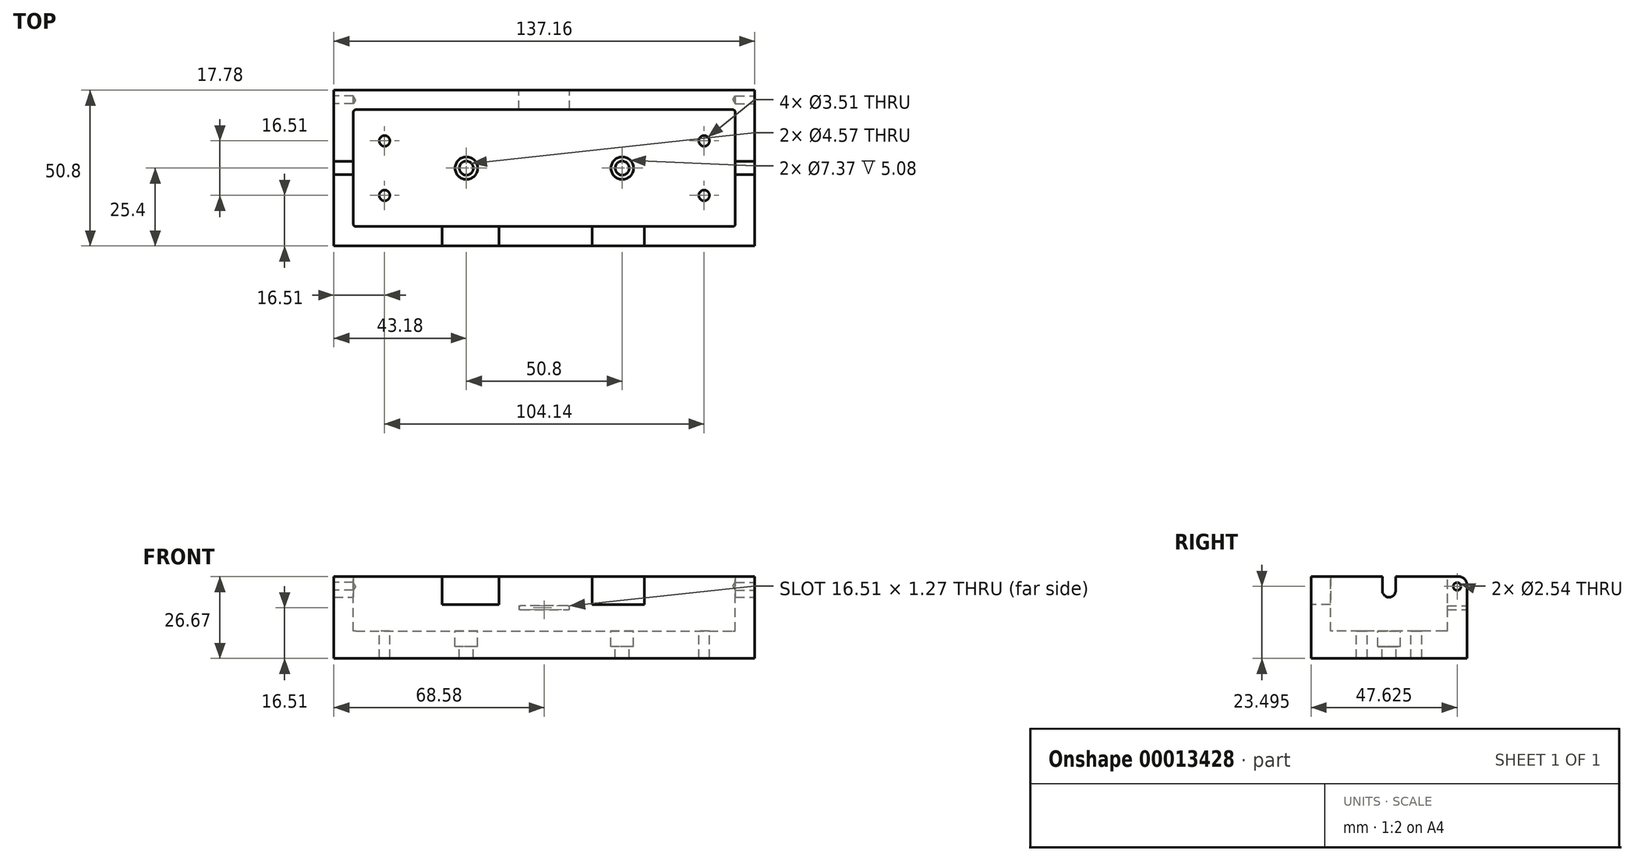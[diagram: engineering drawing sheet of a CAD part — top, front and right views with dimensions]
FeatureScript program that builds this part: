
annotation { "Feature Type Name" : "Feature", "Feature Type Description" : "" }
export const myFeature = defineFeature(function(context is Context, id is Id, definition is map)
    precondition{}
    {
        {
            var Q0;
            Q0=qCreatedBy(makeId("Top.planeOp"),FACE);
            var sketch = newSketch(context, id + "F0", { "sketchPlane" : qUnion([Q0])});
            skLineSegment(sketch, "E0.bottom", {"start": v(0, 50.8) * mm, "end": v(137.16, 50.8) * mm});
            skLineSegment(sketch, "E0.top", {"start": v(0, 0) * mm, "end": v(137.16, 0) * mm});
            skLineSegment(sketch, "E0.left", {"start": v(0, 50.8) * mm, "end": v(0, 0) * mm});
            skLineSegment(sketch, "E0.right", {"start": v(137.16, 50.8) * mm, "end": v(137.16, 0) * mm});
            skSolve(sketch);
        }
        {
            var Q0;
            Q0 = qSketchRegion(id + "F0", true);
            extrude(context, id + "F1", {"entities" : qUnion([Q0]), "depth" : 26.67 * mm});
        }
        {
            var Q0;
            Q0=makeQuery(id+"F1.opExtrude","CAP_FACE",FACE,{"disambiguationData":[OSD([sQuery(id+"F0.wireOp",EDGE,"E0.bottom"),sQuery(id+"F0.wireOp",EDGE,"E0.top"),sQuery(id+"F0.wireOp",EDGE,"E0.left"),sQuery(id+"F0.wireOp",EDGE,"E0.right")])],"isStart":false});
            var sketch = newSketch(context, id + "F2", { "sketchPlane" : qUnion([Q0])});
            skLineSegment(sketch, "E1.bottom", {"start": v(7.16, 44.45) * mm, "end": v(130, 44.45) * mm});
            skLineSegment(sketch, "E1.top", {"start": v(7.16, 6.35) * mm, "end": v(130, 6.35) * mm});
            skLineSegment(sketch, "E1.left", {"start": v(6.35, 43.64) * mm, "end": v(6.35, 7.16) * mm});
            skLineSegment(sketch, "E1.right", {"start": v(130.8, 43.64) * mm, "end": v(130.8, 7.16) * mm});
            skPoint(sketch, "E2.visualSharp", {"position": v(6.35, 44.45) * mm});
            skArc(sketch, "E2.filletArc", {"start": v(7.16, 44.45) * mm, "mid": v(6.59, 44.21) * mm, "end": v(6.35, 43.64) * mm});
            skPoint(sketch, "E3.visualSharp", {"position": v(6.35, 6.35) * mm});
            skArc(sketch, "E3.filletArc", {"start": v(6.35, 7.16) * mm, "mid": v(6.59, 6.59) * mm, "end": v(7.16, 6.35) * mm});
            skPoint(sketch, "E4.visualSharp", {"position": v(130.8, 44.45) * mm});
            skArc(sketch, "E4.filletArc", {"start": v(130.8, 43.64) * mm, "mid": v(130.57, 44.21) * mm, "end": v(130, 44.45) * mm});
            skPoint(sketch, "E5.visualSharp", {"position": v(130.8, 6.35) * mm});
            skArc(sketch, "E5.filletArc", {"start": v(130, 6.35) * mm, "mid": v(130.57, 6.59) * mm, "end": v(130.8, 7.16) * mm});
            skSolve(sketch);
        }
        {
            var Q0;
            Q0 = qSketchRegion(id + "F2", true);
            extrude(context, id + "F3", {"entities" : qUnion([Q0]), "operationType" : NewBodyOperationType.REMOVE, "oppositeDirection" : true, "depth" : 17.78 * mm});
        }
        {
            var Q0;
            Q0=makeQuery(id+"F1.opExtrude","SWEPT_FACE",FACE,{"disambiguationData":[OSD([sQuery(id+"F0.wireOp",EDGE,"E0.right")])]});
            var sketch = newSketch(context, id + "F4", { "sketchPlane" : qUnion([Q0])});
            skArc(sketch, "E6", {"start": v(23.24, 22.1) * mm, "mid": v(25.4, 19.94) * mm, "end": v(27.56, 22.1) * mm});
            skLineSegment(sketch, "E7.top", {"start": v(27.56, 26.67) * mm, "end": v(23.24, 26.67) * mm});
            skLineSegment(sketch, "E7.left", {"start": v(27.56, 22.1) * mm, "end": v(27.56, 26.67) * mm});
            skLineSegment(sketch, "E7.right", {"start": v(23.24, 22.1) * mm, "end": v(23.24, 26.67) * mm});
            skSolve(sketch);
        }
        {
            var Q0;
            Q0 = qSketchRegion(id + "F4", true);
            extrude(context, id + "F5", {"entities" : qUnion([Q0]), "operationType" : NewBodyOperationType.REMOVE, "endBound" : BoundingType.THROUGH_ALL, "oppositeDirection" : true, "depth" : 25.4 * mm});
        }
        {
            var Q0;
            Q0=makeQuery(id+"F3.boolean.opBoolean","COPY",FACE,{"derivedFrom":makeQuery(id+"F3.opExtrude","CAP_FACE",FACE,{"disambiguationData":[OSD([sQuery(id+"F2.wireOp",EDGE,"E1.bottom"),sQuery(id+"F2.wireOp",EDGE,"E1.top"),sQuery(id+"F2.wireOp",EDGE,"E1.left"),sQuery(id+"F2.wireOp",EDGE,"E1.right"),sQuery(id+"F2.wireOp",EDGE,"E2.filletArc"),sQuery(id+"F2.wireOp",EDGE,"E3.filletArc"),sQuery(id+"F2.wireOp",EDGE,"E4.filletArc"),sQuery(id+"F2.wireOp",EDGE,"E5.filletArc")])],"isStart":false})});
            var sketch = newSketch(context, id + "F6", { "sketchPlane" : qUnion([Q0])});
            skPoint(sketch, "E8", {"position": v(16.51, 34.29) * mm});
            skPoint(sketch, "E9", {"position": v(16.51, 16.5) * mm});
            skPoint(sketch, "E10", {"position": v(120.65, 16.51) * mm});
            skPoint(sketch, "E11", {"position": v(120.65, 34.3) * mm});
            skSolve(sketch);
        }
        {
            var Q0;
            Q0=sQuery(id+"F6.wireOp",VERTEX,"E8");
            var Q1;
            Q1=sQuery(id+"F6.wireOp",VERTEX,"E9");
            var Q2;
            Q2=sQuery(id+"F6.wireOp",VERTEX,"E11");
            var Q3;
            Q3=sQuery(id+"F6.wireOp",VERTEX,"E10");
            var Q4;
            Q4=makeQuery(id+"F1.opExtrude","SWEPT_BODY",BODY,{"disambiguationData":[OSD([sQuery(id+"F0.wireOp",EDGE,"E0.bottom"),sQuery(id+"F0.wireOp",EDGE,"E0.top"),sQuery(id+"F0.wireOp",EDGE,"E0.left"),sQuery(id+"F0.wireOp",EDGE,"E0.right")])]});
            hole(context, id + "F7", {"style" : HoleStyle.SIMPLE, "holeDiameter" : 3.5 * mm, "endStyle" : HoleEndStyle.THROUGH, "locations" : qUnion([Q0, Q1, Q2, Q3]), "scope" : qUnion([Q4])});
        }
        {
            var Q0;
            Q0=makeQuery(id+"F3.boolean.opBoolean","COPY",FACE,{"derivedFrom":makeQuery(id+"F3.opExtrude","CAP_FACE",FACE,{"disambiguationData":[OSD([sQuery(id+"F2.wireOp",EDGE,"E1.bottom"),sQuery(id+"F2.wireOp",EDGE,"E1.top"),sQuery(id+"F2.wireOp",EDGE,"E1.left"),sQuery(id+"F2.wireOp",EDGE,"E1.right"),sQuery(id+"F2.wireOp",EDGE,"E2.filletArc"),sQuery(id+"F2.wireOp",EDGE,"E3.filletArc"),sQuery(id+"F2.wireOp",EDGE,"E4.filletArc"),sQuery(id+"F2.wireOp",EDGE,"E5.filletArc")])],"isStart":false})});
            var sketch = newSketch(context, id + "F8", { "sketchPlane" : qUnion([Q0])});
            skPoint(sketch, "E12", {"position": v(43.18, 25.4) * mm});
            skPoint(sketch, "E13", {"position": v(93.98, 25.4) * mm});
            skSolve(sketch);
        }
        {
            var Q0;
            Q0=sQuery(id+"F8.wireOp",VERTEX,"E12");
            var Q1;
            Q1=sQuery(id+"F8.wireOp",VERTEX,"E13");
            var Q2;
            Q2=makeQuery(id+"F1.opExtrude","SWEPT_BODY",BODY,{"disambiguationData":[OSD([sQuery(id+"F0.wireOp",EDGE,"E0.bottom"),sQuery(id+"F0.wireOp",EDGE,"E0.top"),sQuery(id+"F0.wireOp",EDGE,"E0.left"),sQuery(id+"F0.wireOp",EDGE,"E0.right")])]});
            hole(context, id + "F9", {"style" : HoleStyle.C_BORE, "holeDiameter" : 4.57 * mm, "cBoreDiameter" : 7.37 * mm, "cBoreDepth" : 5.08 * mm, "endStyle" : HoleEndStyle.THROUGH, "locations" : qUnion([Q0, Q1]), "scope" : qUnion([Q2])});
        }
        {
            var Q0;
            Q0=makeQuery(id+"F1.opExtrude","SWEPT_FACE",FACE,{"disambiguationData":[OSD([sQuery(id+"F0.wireOp",EDGE,"E0.bottom")])]});
            var sketch = newSketch(context, id + "F10", { "sketchPlane" : qUnion([Q0])});
            skPoint(sketch, "E14", {"position": v(-60.96, 16.5) * mm});
            skPoint(sketch, "E15.1.0.0", {"position": v(-76.2, 16.5) * mm});
            skLineSegment(sketch, "E15.direction1", {"start": v(-60.96, 16.5) * mm, "end": v(-76.2, 16.5) * mm, "construction": true});
            skArc(sketch, "E16", {"start": v(-60.96, 15.87) * mm, "mid": v(-60.33, 16.5) * mm, "end": v(-60.96, 17.14) * mm});
            skArc(sketch, "E17", {"start": v(-76.2, 17.14) * mm, "mid": v(-76.83, 16.5) * mm, "end": v(-76.2, 15.87) * mm});
            skLineSegment(sketch, "E18", {"start": v(-76.2, 17.14) * mm, "end": v(-60.96, 17.14) * mm});
            skLineSegment(sketch, "E19", {"start": v(-60.96, 15.87) * mm, "end": v(-76.2, 15.87) * mm});
            skSolve(sketch);
        }
        {
            var Q0;
            Q0 = qSketchRegion(id + "F10", true);
            extrude(context, id + "F11", {"entities" : qUnion([Q0]), "operationType" : NewBodyOperationType.REMOVE, "endBound" : BoundingType.UP_TO_NEXT, "oppositeDirection" : true, "depth" : 25.4 * mm});
        }
        {
            var Q0;
            Q0=makeQuery(id+"F1.opExtrude","SWEPT_FACE",FACE,{"disambiguationData":[OSD([sQuery(id+"F0.wireOp",EDGE,"E0.top")])]});
            var sketch = newSketch(context, id + "F12", { "sketchPlane" : qUnion([Q0])});
            skLineSegment(sketch, "E20.bottom", {"start": v(35.26, 17.53) * mm, "end": v(45.42, 17.53) * mm});
            skLineSegment(sketch, "E21.right", {"start": v(101.14, 20.07) * mm, "end": v(101.14, 26.67) * mm});
            skLineSegment(sketch, "E20.right", {"start": v(45.42, 17.53) * mm, "end": v(45.42, 26.67) * mm});
            skLineSegment(sketch, "E21.left", {"start": v(88.44, 20.07) * mm, "end": v(88.44, 26.67) * mm});
            skLineSegment(sketch, "E21.top", {"start": v(88.44, 26.67) * mm, "end": v(101.14, 26.67) * mm});
            skLineSegment(sketch, "E21.bottom", {"start": v(88.44, 20.07) * mm, "end": v(101.14, 20.07) * mm});
            skLineSegment(sketch, "E20.left", {"start": v(35.26, 17.53) * mm, "end": v(35.26, 26.67) * mm});
            skLineSegment(sketch, "E20.top", {"start": v(35.26, 26.67) * mm, "end": v(45.42, 26.67) * mm});
            skSolve(sketch);
        }
        {
            var Q0;
            Q0 = qSketchRegion(id + "F12", true);
            extrude(context, id + "F13", {"entities" : qUnion([Q0]), "operationType" : NewBodyOperationType.REMOVE, "endBound" : BoundingType.UP_TO_NEXT, "oppositeDirection" : true, "depth" : 25.4 * mm});
        }
        {
            var Q0;
            {var subQ0=sQuery(id+"F0.wireOp",EDGE,"E0.top");var subQ1=sQuery(id+"F0.wireOp",EDGE,"E0.left");var subQ2=sQuery(id+"F0.wireOp",EDGE,"E0.right");var subQ7=makeQuery(id+"F1.opExtrude","SWEPT_FACE",FACE,{"disambiguationData":[OSD([subQ1])]});var subQ8=makeQuery(id+"F1.opExtrude","SWEPT_FACE",FACE,{"disambiguationData":[OSD([subQ0])]});Q0=makeQuery(id+"F13.boolean.opBoolean","SPLIT",FACE,{"disambiguationData":[TD([subQ7])],"derivedFrom":makeQuery(id+"F5.boolean.opBoolean","SPLIT",FACE,{"disambiguationData":[TD([subQ8])],"derivedFrom":makeQuery(id+"F1.opExtrude","CAP_FACE",FACE,{"disambiguationData":[OSD([sQuery(id+"F0.wireOp",EDGE,"E0.bottom"),subQ0,subQ1,subQ2])],"isStart":false})})});}
            var sketch = newSketch(context, id + "F14", { "sketchPlane" : qUnion([Q0])});
            skLineSegment(sketch, "E22.bottom", {"start": v(43.66, 6.35) * mm, "end": v(53.82, 6.35) * mm});
            skLineSegment(sketch, "E22.top", {"start": v(43.66, 0) * mm, "end": v(53.82, 0) * mm});
            skLineSegment(sketch, "E22.left", {"start": v(43.66, 6.35) * mm, "end": v(43.66, 0) * mm});
            skLineSegment(sketch, "E22.right", {"start": v(53.82, 6.35) * mm, "end": v(53.82, 0) * mm});
            skSolve(sketch);
        }
        {
            var Q0;
            Q0 = qSketchRegion(id + "F14", true);
            var Q1;
            Q1=makeQuery(id+"F13.boolean.opBoolean","COPY",FACE,{"derivedFrom":makeQuery(id+"F13.opExtrude","SWEPT_FACE",FACE,{"disambiguationData":[OSD([sQuery(id+"F12.wireOp",EDGE,"E20.bottom")])]})});
            extrude(context, id + "F15", {"entities" : qUnion([Q0]), "operationType" : NewBodyOperationType.REMOVE, "endBound" : BoundingType.UP_TO_SURFACE, "oppositeDirection" : true, "endBoundEntityFace" : qUnion([Q1]), "depth" : 25.4 * mm});
        }
        {
            var Q0;
            {var subQ0=sQuery(id+"F0.wireOp",EDGE,"E0.top");var subQ1=sQuery(id+"F0.wireOp",EDGE,"E0.left");var subQ2=sQuery(id+"F0.wireOp",EDGE,"E0.right");var subQ4=makeQuery(id+"F1.opExtrude","SWEPT_FACE",FACE,{"disambiguationData":[OSD([subQ0])]});Q0=makeQuery(id+"F13.boolean.opBoolean","SPLIT",FACE,{"disambiguationData":[TD([makeQuery(id+"F13.opExtrude","SWEPT_FACE",FACE,{"disambiguationData":[OSD([sQuery(id+"F12.wireOp",EDGE,"E20.right")])]})])],"derivedFrom":makeQuery(id+"F5.boolean.opBoolean","SPLIT",FACE,{"disambiguationData":[TD([subQ4])],"derivedFrom":makeQuery(id+"F1.opExtrude","CAP_FACE",FACE,{"disambiguationData":[OSD([sQuery(id+"F0.wireOp",EDGE,"E0.bottom"),subQ0,subQ1,subQ2])],"isStart":false})})});}
            var sketch = newSketch(context, id + "F16", { "sketchPlane" : qUnion([Q0])});
            skLineSegment(sketch, "E23.bottom", {"start": v(84.15, 9.47) * mm, "end": v(101.14, 9.47) * mm});
            skLineSegment(sketch, "E23.top", {"start": v(84.15, 0) * mm, "end": v(101.14, 0) * mm});
            skLineSegment(sketch, "E23.left", {"start": v(84.15, 9.47) * mm, "end": v(84.15, 0) * mm});
            skLineSegment(sketch, "E23.right", {"start": v(101.14, 9.47) * mm, "end": v(101.14, 0) * mm});
            skSolve(sketch);
        }
        {
            var Q0;
            Q0 = qSketchRegion(id + "F16", true);
            var Q1;
            Q1=makeQuery(id+"F15.boolean.opBoolean","MERGE",FACE,{"derivedFrom":[makeQuery(id+"F13.boolean.opBoolean","COPY",FACE,{"derivedFrom":makeQuery(id+"F13.opExtrude","SWEPT_FACE",FACE,{"disambiguationData":[OSD([sQuery(id+"F12.wireOp",EDGE,"E20.bottom")])]})}),makeQuery(id+"F15.opExtrude","CAP_FACE",FACE,{"disambiguationData":[OSD([sQuery(id+"F14.wireOp",EDGE,"E22.bottom"),sQuery(id+"F14.wireOp",EDGE,"E22.top"),sQuery(id+"F14.wireOp",EDGE,"E22.left"),sQuery(id+"F14.wireOp",EDGE,"E22.right")])],"isStart":false})]});
            extrude(context, id + "F17", {"entities" : qUnion([Q0]), "operationType" : NewBodyOperationType.REMOVE, "endBound" : BoundingType.UP_TO_SURFACE, "oppositeDirection" : true, "endBoundEntityFace" : qUnion([Q1]), "depth" : 25.4 * mm});
        }
        {
            var Q0;
            Q0=makeQuery(id+"F1.opExtrude","SWEPT_FACE",FACE,{"disambiguationData":[OSD([sQuery(id+"F0.wireOp",EDGE,"E0.right")])]});
            var sketch = newSketch(context, id + "F18", { "sketchPlane" : qUnion([Q0])});
            skPoint(sketch, "E24", {"position": v(47.62, 23.5) * mm});
            skSolve(sketch);
        }
        {
            var Q0;
            Q0=sQuery(id+"F18.wireOp",VERTEX,"E24");
            var Q1;
            Q1=makeQuery(id+"F1.opExtrude","SWEPT_BODY",BODY,{"disambiguationData":[OSD([sQuery(id+"F0.wireOp",EDGE,"E0.bottom"),sQuery(id+"F0.wireOp",EDGE,"E0.top"),sQuery(id+"F0.wireOp",EDGE,"E0.left"),sQuery(id+"F0.wireOp",EDGE,"E0.right")])]});
            hole(context, id + "F19", {"style" : HoleStyle.SIMPLE, "holeDiameter" : 2.54 * mm, "endStyle" : HoleEndStyle.BLIND, "holeDepth" : 6.35 * mm, "locations" : qUnion([Q0]), "scope" : qUnion([Q1])});
        }
        {
            var Q0;
            Q0=makeQuery(id+"F1.opExtrude","SWEPT_FACE",FACE,{"disambiguationData":[OSD([sQuery(id+"F0.wireOp",EDGE,"E0.left")])]});
            var sketch = newSketch(context, id + "F20", { "sketchPlane" : qUnion([Q0])});
            skPoint(sketch, "E25", {"position": v(-47.63, 23.5) * mm});
            skSolve(sketch);
        }
        {
            var Q0;
            Q0=sQuery(id+"F20.wireOp",VERTEX,"E25");
            var Q1;
            Q1=makeQuery(id+"F1.opExtrude","SWEPT_BODY",BODY,{"disambiguationData":[OSD([sQuery(id+"F0.wireOp",EDGE,"E0.bottom"),sQuery(id+"F0.wireOp",EDGE,"E0.top"),sQuery(id+"F0.wireOp",EDGE,"E0.left"),sQuery(id+"F0.wireOp",EDGE,"E0.right")])]});
            hole(context, id + "F21", {"style" : HoleStyle.SIMPLE, "holeDiameter" : 2.54 * mm, "endStyle" : HoleEndStyle.BLIND, "holeDepth" : 6.35 * mm, "locations" : qUnion([Q0]), "scope" : qUnion([Q1])});
        }
        {
            var Q0;
            Q0=makeQuery(id+"F1.opExtrude","CAP_EDGE",EDGE,{"disambiguationData":[OSD([sQuery(id+"F0.wireOp",EDGE,"E0.bottom")])],"isStart":false});
            fillet(context, id + "F22", {"entities" : qUnion([Q0]), "radius" : 2.54 * mm, "tangentPropagation" : true, "allowEdgeOverflow" : false});
        }
    });
